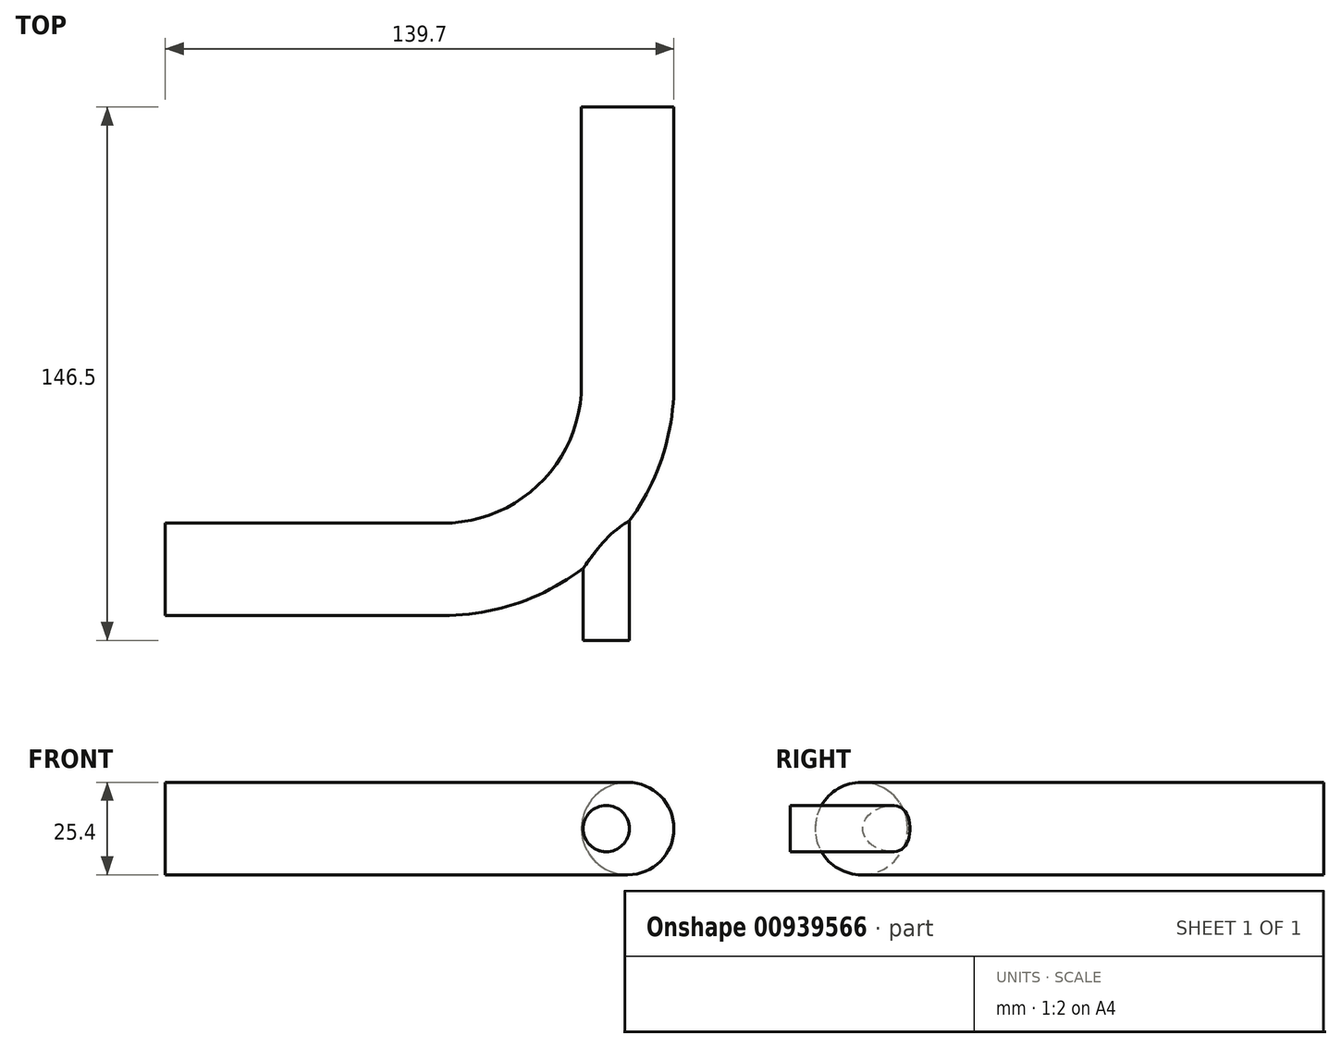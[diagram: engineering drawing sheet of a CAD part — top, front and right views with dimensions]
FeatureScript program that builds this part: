
annotation { "Feature Type Name" : "Feature", "Feature Type Description" : "" }
export const myFeature = defineFeature(function(context is Context, id is Id, definition is map)
    precondition{}
    {
        {
            var Q0;
            Q0=qCreatedBy(makeId("Top.planeOp"),FACE);
            var sketch = newSketch(context, id + "F0", { "sketchPlane" : qUnion([Q0])});
            skLineSegment(sketch, "E0", {"start": v(0, 0) * mm, "end": v(76.2, 0) * mm});
            skArc(sketch, "E1", {"start": v(76.2, 0) * mm, "mid": v(112.12, 14.88) * mm, "end": v(127, 50.8) * mm});
            skLineSegment(sketch, "E2", {"start": v(127, 50.8) * mm, "end": v(127, 127) * mm});
            skLineSegment(sketch, "E3", {"start": v(76.2, 50.8) * mm, "end": v(172.34, -45.34) * mm, "construction": true});
            skSolve(sketch);
        }
        {
            var Q0;
            Q0=qCreatedBy(makeId("Right.planeOp"),FACE);
            var sketch = newSketch(context, id + "F1", { "sketchPlane" : qUnion([Q0])});
            skCircle(sketch, "E4", {"center": v(0, 0) * mm, "radius": 12.7 * mm});
            skSolve(sketch);
        }
        {
            var Q0;
            Q0=makeQuery(id+"F1.imprint","IMPRINT",FACE,{"disambiguationData":[TD([[makeQuery(id+"F1.imprint","IMPRINT",EDGE,{"derivedFrom":sQuery(id+"F1.wireOp",EDGE,"E4")}),1.0]])]});
            var Q1;
            Q1=sQuery(id+"F0.wireOp",EDGE,"E0");
            var Q2;
            Q2=sQuery(id+"F0.wireOp",EDGE,"E1");
            var Q3;
            Q3=sQuery(id+"F0.wireOp",EDGE,"E2");
            sweep(context, id + "F2", {"profiles" : qUnion([Q0]), "path" : qUnion([Q1, Q2, Q3])});
        }
        {
            var Q0;
            Q0=qCreatedBy(makeId("Top.planeOp"),FACE);
            var sketch = newSketch(context, id + "F3", { "sketchPlane" : qUnion([Q0])});
            skLineSegment(sketch, "E5.0", {"start": v(114.3, 50.8) * mm, "end": v(139.7, 50.8) * mm});
            skLineSegment(sketch, "E6.0", {"start": v(76.2, 12.7) * mm, "end": v(76.2, -12.7) * mm});
            skLineSegment(sketch, "E7", {"start": v(76.2, 50.8) * mm, "end": v(136.6, -9.6) * mm, "construction": true});
            skPoint(sketch, "E8.orphan", {"position": v(114.3, 12.7) * mm});
            skArc(sketch, "E9", {"start": v(114.3, 50.8) * mm, "mid": v(103.14, 23.86) * mm, "end": v(76.2, 12.7) * mm});
            skArc(sketch, "E10", {"start": v(76.2, -12.7) * mm, "mid": v(121.1, 5.9) * mm, "end": v(139.7, 50.8) * mm});
            skLineSegment(sketch, "E11", {"start": v(121.1, 5.9) * mm, "end": v(121.1, -19.5) * mm, "construction": true});
            skSolve(sketch);
        }
        {
            var Q0;
            Q0=sQuery(id+"F3.wireOp",VERTEX,"E11.end");
            var Q1;
            Q1=qCreatedBy(makeId("Front.planeOp"),FACE);
            cPlane(context, id + "F4", {"entities" : qUnion([Q0, Q1]), "cplaneType" : CPlaneType.PLANE_POINT, "offset" : 25.4 * mm, "width" : 152.4 * mm, "height" : 152.4 * mm});
        }
        {
            var Q0;
            Q0=qCreatedBy(id+"F4.planeOp",FACE);
            var sketch = newSketch(context, id + "F5", { "sketchPlane" : qUnion([Q0])});
            skPoint(sketch, "E12.0", {"position": v(121.1, 0) * mm});
            skCircle(sketch, "E13", {"center": v(121.1, 0) * mm, "radius": 6.35 * mm});
            skSolve(sketch);
        }
        {
            var Q0;
            Q0=makeQuery(id+"F5.imprint","IMPRINT",FACE,{"disambiguationData":[TD([[makeQuery(id+"F5.imprint","IMPRINT",EDGE,{"derivedFrom":sQuery(id+"F5.wireOp",EDGE,"E13")}),1.0]])]});
            extrude(context, id + "F6", {"entities" : qUnion([Q0]), "operationType" : NewBodyOperationType.ADD, "endBound" : BoundingType.UP_TO_NEXT, "oppositeDirection" : true, "depth" : 42.93 * mm, "offsetDistance" : 25.4 * mm});
        }
    });
